# Revit family: SOEB13
name_source: partatom
category: Plumbing Fixtures
revit_build: Autodesk Revit 2015 (Build: 20140903_1530(x64)
units: mm (PartAtom-declared; Revit-internal decimal feet)

## types (4) — shared parameters
Chrome = Chrome
Glass = Glass
H = 1500 mm  [stored 4.92126 ft]
Manufacturer = SanSwiss
Metal = Aluminum
Model = SOEB13
Seal = Seal
Type Comments = SOLINO
URL = www.sanswiss.com
zero-valued in all types: Number of elements, Width fixed panel 2

## per-type parameters (varying)
| type | A1 | B1 | C1 | D | L1 | door | holder | holder type |
| 900 | 900 mm | 350 mm  [stored 1.14829 ft] | 550 mm | 300 mm | 900 mm | SOL1_G : C=550 | holder : B=350,D=300 | holder : B=350,D=300 |
| 1000 | 1000 mm  [stored 3.28084 ft] | 350 mm  [stored 1.14829 ft] | 650 mm  [stored 2.13255 ft] | 300 mm | 1000 mm  [stored 3.28084 ft] | SOL1_G : C=650 | holder : B=350,D=300 | holder : B=350,D=300 |
| 1200 | 1200 mm | 400 mm  [stored 1.31234 ft] | 800 mm  [stored 2.62467 ft] | 350 mm  [stored 1.14829 ft] | 1200 mm | SOL1_G : C=800 | holder : B=400,D=350 | holder : B=400,D=350 |
| 1100 | 1100 mm | 400 mm  [stored 1.31234 ft] | 700 mm  [stored 2.29659 ft] | 350 mm  [stored 1.14829 ft] | 1100 mm | SOL1_G : C=700 | holder : B=400,D=350 | holder : B=400,D=350 |

note: [stored X ft] marks values corroborated as IEEE doubles in the binary element streams (Revit-internal decimal feet)

## geometry (parser evidence)
native form markers: Sweep x9
no freeform markers — native parametric forms only
